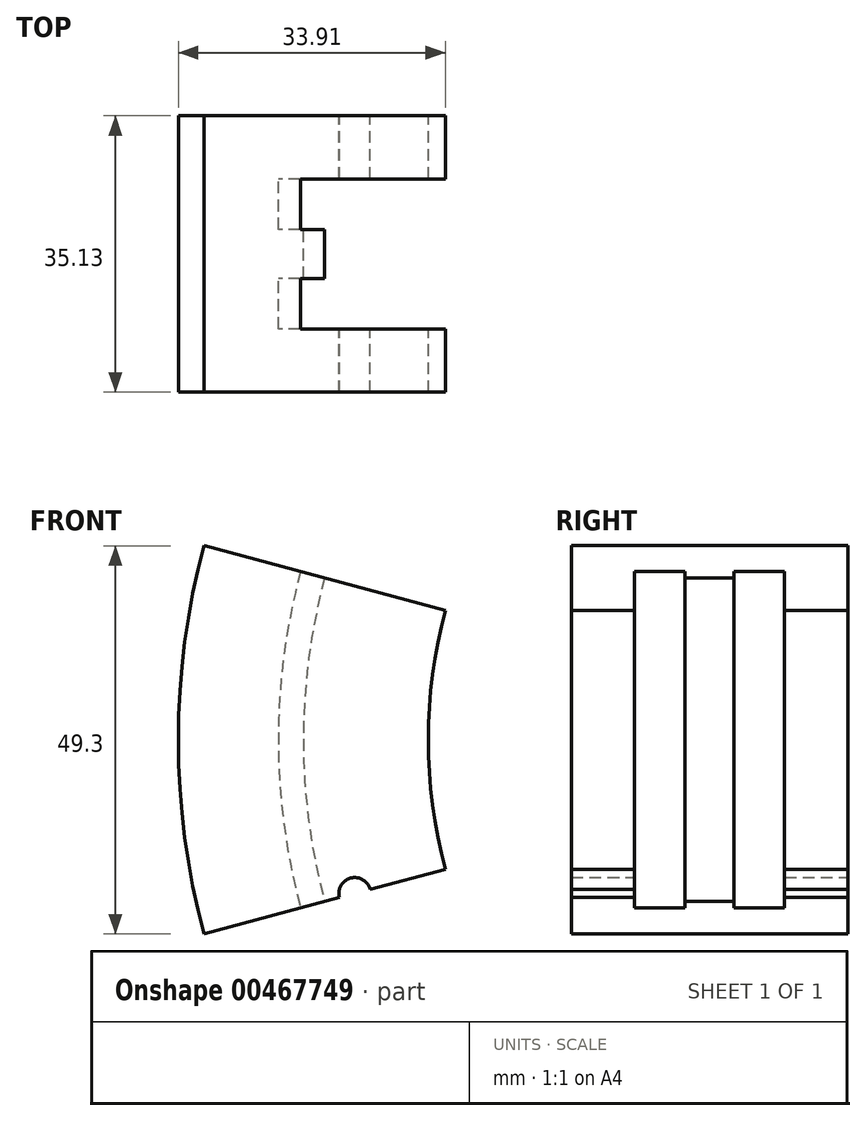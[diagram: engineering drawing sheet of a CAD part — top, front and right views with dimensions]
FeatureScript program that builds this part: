
annotation { "Feature Type Name" : "Feature", "Feature Type Description" : "" }
export const myFeature = defineFeature(function(context is Context, id is Id, definition is map)
    precondition{}
    {
        {
            var Q0;
            Q0=qCreatedBy(makeId("Front.planeOp"),FACE);
            var sketch = newSketch(context, id + "F0", { "sketchPlane" : qUnion([Q0])});
            skArc(sketch, "E0", {"start": v(-73.6, 19.72) * mm, "mid": v(-76.2, 0) * mm, "end": v(-73.6, -19.72) * mm});
            skLineSegment(sketch, "E1", {"start": v(-73.6, 19.72) * mm, "end": v(0, 0) * mm, "construction": true});
            skLineSegment(sketch, "E2", {"start": v(-73.6, -19.72) * mm, "end": v(0, 0) * mm, "construction": true});
            skSolve(sketch);
        }
        {
            var Q0;
            Q0=qCreatedBy(makeId("Top.planeOp"),FACE);
            var sketch = newSketch(context, id + "F1", { "sketchPlane" : qUnion([Q0])});
            skLineSegment(sketch, "E3", {"start": v(-95.25, 0) * mm, "end": v(-95.25, 17.56) * mm});
            skLineSegment(sketch, "E4", {"start": v(-95.25, 17.56) * mm, "end": v(-63.5, 17.56) * mm});
            skLineSegment(sketch, "E5", {"start": v(-63.5, 17.56) * mm, "end": v(-63.5, 9.54) * mm});
            skLineSegment(sketch, "E6", {"start": v(-63.5, 9.54) * mm, "end": v(-82.55, 9.54) * mm});
            skLineSegment(sketch, "E7", {"start": v(0, 0) * mm, "end": v(-121.04, 0) * mm, "construction": true});
            skLineSegment(sketch, "E8.MirrorCS", {"start": v(-95.25, 0) * mm, "end": v(-95.25, -17.56) * mm});
            skLineSegment(sketch, "E9.MirrorCS", {"start": v(-95.25, -17.56) * mm, "end": v(-63.5, -17.56) * mm});
            skLineSegment(sketch, "E10.MirrorCS", {"start": v(-63.5, -17.56) * mm, "end": v(-63.5, -9.54) * mm});
            skLineSegment(sketch, "E11.MirrorCS", {"start": v(-63.5, -9.54) * mm, "end": v(-82.55, -9.54) * mm});
            skLineSegment(sketch, "E12", {"start": v(-82.55, 3.11) * mm, "end": v(-79.38, 3.11) * mm});
            skLineSegment(sketch, "E13", {"start": v(-79.38, 3.11) * mm, "end": v(-79.38, 0) * mm});
            skLineSegment(sketch, "E14", {"start": v(-82.55, 9.54) * mm, "end": v(-82.55, 3.11) * mm});
            skLineSegment(sketch, "E15.MirrorCS", {"start": v(-82.55, -9.54) * mm, "end": v(-82.55, -3.11) * mm});
            skLineSegment(sketch, "E16.MirrorCS", {"start": v(-82.55, -3.11) * mm, "end": v(-79.38, -3.11) * mm});
            skLineSegment(sketch, "E17.MirrorCS", {"start": v(-79.38, -3.11) * mm, "end": v(-79.38, 0) * mm});
            skSolve(sketch);
        }
        {
            var Q0;
            Q0=makeQuery(id+"F1.imprint","IMPRINT",FACE,{"disambiguationData":[TD([[makeQuery(id+"F1.imprint","IMPRINT",EDGE,{"derivedFrom":sQuery(id+"F1.wireOp",EDGE,"E3")}),-1.0]])]});
            var Q1;
            Q1=sQuery(id+"F0.wireOp",EDGE,"E0");
            sweep(context, id + "F2", {"profiles" : qUnion([Q0]), "path" : qUnion([Q1])});
        }
        {
            var Q0;
            Q0=makeQuery(id+"F2.opSweep","CAP_VERTEX",VERTEX,{"disambiguationData":[OSD([sQuery(id+"F0.wireOp",EDGE,"E0"),sQuery(id+"F1.wireOp",EDGE,"E9.MirrorCS"),sQuery(id+"F1.wireOp",EDGE,"E10.MirrorCS")])],"isStart":true});
            var Q1;
            Q1=makeQuery(id+"F2.opSweep","CAP_VERTEX",VERTEX,{"disambiguationData":[OSD([sQuery(id+"F0.wireOp",EDGE,"E0"),sQuery(id+"F1.wireOp",EDGE,"E4"),sQuery(id+"F1.wireOp",EDGE,"E5")])],"isStart":false});
            var Q2;
            Q2=makeQuery(id+"F2.opSweep","CAP_VERTEX",VERTEX,{"disambiguationData":[OSD([sQuery(id+"F0.wireOp",EDGE,"E0"),sQuery(id+"F1.wireOp",EDGE,"E9.MirrorCS"),sQuery(id+"F1.wireOp",EDGE,"E10.MirrorCS")])],"isStart":false});
            cPlane(context, id + "F3", {"entities" : qUnion([Q0, Q1, Q2]), "cplaneType" : CPlaneType.THREE_POINT, "offset" : 25.4 * mm, "width" : 152.4 * mm, "height" : 152.4 * mm});
        }
        {
            var Q0;
            Q0=qCreatedBy(id+"F3.planeOp",FACE);
            var sketch = newSketch(context, id + "F4", { "sketchPlane" : qUnion([Q0])});
            skCircle(sketch, "E18", {"center": v(0, 0) * mm, "radius": 3.97 * mm});
            skSolve(sketch);
        }
        {
            var Q0;
            Q0 = qSketchRegion(id + "F4", true);
            extrude(context, id + "F5", {"entities" : qUnion([Q0]), "operationType" : NewBodyOperationType.REMOVE, "endBound" : BoundingType.THROUGH_ALL, "oppositeDirection" : true, "depth" : 25.4 * mm});
        }
        {
            var Q0;
            Q0=makeQuery(id+"F2.opSweep","SWEPT_FACE",FACE,{"disambiguationData":[OSD([sQuery(id+"F0.wireOp",EDGE,"E0"),sQuery(id+"F1.wireOp",EDGE,"E9.MirrorCS")])]});
            var sketch = newSketch(context, id + "F6", { "sketchPlane" : qUnion([Q0])});
            skArc(sketch, "E19", {"start": v(-75.41, 0) * mm, "mid": v(-72.84, -19.52) * mm, "end": v(-65.3, -37.7) * mm, "construction": true});
            skPoint(sketch, "E20", {"position": v(-72.84, -19.52) * mm});
            skArc(sketch, "E21", {"start": v(-77.47, 0) * mm, "mid": v(-74.83, -20.05) * mm, "end": v(-67.1, -38.73) * mm, "construction": true});
            skSolve(sketch);
        }
        {
            var Q0;
            Q0=sQuery(id+"F6.wireOp",VERTEX,"E20");
            var Q1;
            Q1=makeQuery(id+"F2.opSweep","SWEPT_BODY",BODY,{"disambiguationData":[OSD([sQuery(id+"F0.wireOp",EDGE,"E0"),sQuery(id+"F1.wireOp",EDGE,"E3"),sQuery(id+"F1.wireOp",EDGE,"E4"),sQuery(id+"F1.wireOp",EDGE,"E5"),sQuery(id+"F1.wireOp",EDGE,"E6"),sQuery(id+"F1.wireOp",EDGE,"E8.MirrorCS"),sQuery(id+"F1.wireOp",EDGE,"E9.MirrorCS"),sQuery(id+"F1.wireOp",EDGE,"E10.MirrorCS"),sQuery(id+"F1.wireOp",EDGE,"E11.MirrorCS"),sQuery(id+"F1.wireOp",EDGE,"E12"),sQuery(id+"F1.wireOp",EDGE,"E13"),sQuery(id+"F1.wireOp",EDGE,"E14"),sQuery(id+"F1.wireOp",EDGE,"E15.MirrorCS"),sQuery(id+"F1.wireOp",EDGE,"E16.MirrorCS"),sQuery(id+"F1.wireOp",EDGE,"E17.MirrorCS")])]});
            hole(context, id + "F7", {"style" : HoleStyle.SIMPLE, "endStyle" : HoleEndStyle.THROUGH, "standardTappedOrClearance" : lookupTablePath({ "standard" : "ANSI", "engagement" : "75%", "pitch" : "32 tpi", "size" : "#10", "type" : "Tapped" }), "standardBlindInLast" : lookupTablePath({ "standard" : "ANSI", "engagement" : "75%", "pitch" : "32 tpi", "size" : "#10", "type" : "Tapped" }), "holeDiameter" : 4.04 * mm, "showTappedDepth" : true, "isTappedThrough" : true, "tappedDepth" : 12.7 * mm, "tapClearance" : 3, "locations" : qUnion([Q0]), "scope" : qUnion([Q1]), "majorDiameter" : 4.83 * mm, "startStyle" : HoleStartStyle.SKETCH});
        }
    });
